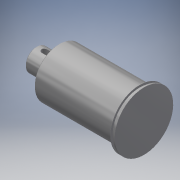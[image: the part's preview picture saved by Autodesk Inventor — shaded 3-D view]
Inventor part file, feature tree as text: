
AUTODESK INVENTOR PART (.ipt)
format: ipt  version: 2019 (Build 230136000, 136)  size: 179,712 bytes
history: native  units: mm
features: other x8, chamfer x2, fillet x1
ambient origin geometry x6: Origin, XZ Plane, XY Plane, X Axis, Y Axis, Z Axis
bodies: Body1 (feature_tree)
feature tree (11):
  other  "實體1"
  other  "迴轉1"
  chamfer  "倒角1"  [1 undecoded]
  fillet  "圓角1"  Radius=10.0mm
  other  "鍵槽1"
  chamfer  "倒角2"  Distance=22.0mm
  other  "扣環槽1"
  other  "起始平面"
  other  "主要草圖"
  other  "iFeature3:1"
  other  "iFeature27:1"
note: 1 required parameter value undecoded (feature->parameter linkage not recoverable at this tier; creation-order binding heuristic only, values carry confidence <= 0.55)
